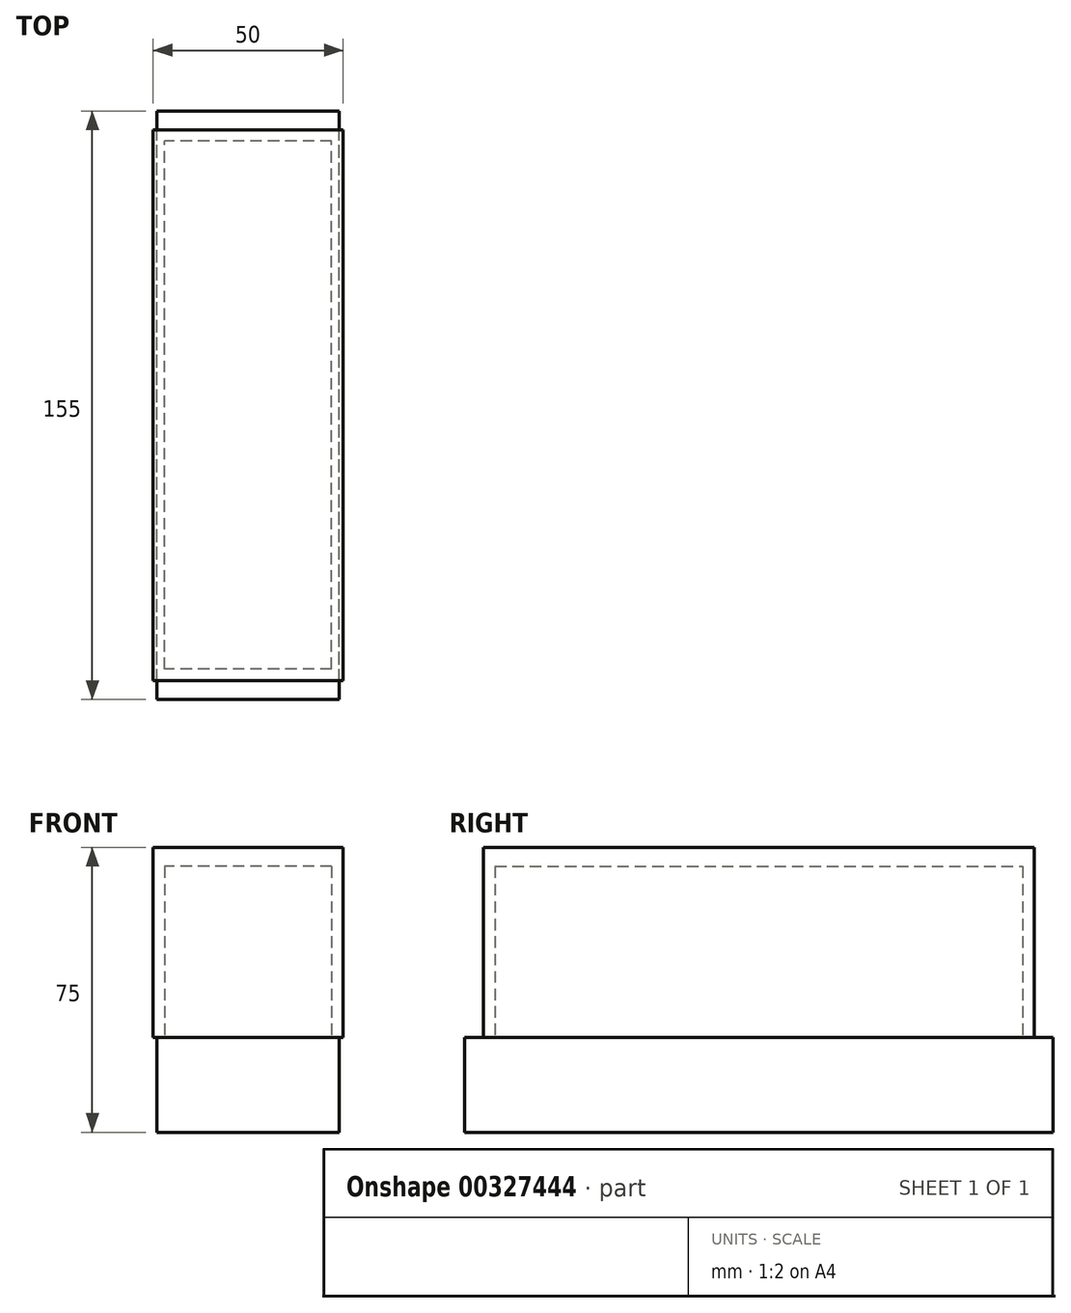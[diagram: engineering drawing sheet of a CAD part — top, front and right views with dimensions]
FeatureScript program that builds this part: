
annotation { "Feature Type Name" : "Feature", "Feature Type Description" : "" }
export const myFeature = defineFeature(function(context is Context, id is Id, definition is map)
    precondition{}
    {
        {
            var Q0;
            Q0=qCreatedBy(makeId("Top.planeOp"),FACE);
            var sketch = newSketch(context, id + "F0", { "sketchPlane" : qUnion([Q0])});
            skLineSegment(sketch, "E0.bottom", {"start": v(22, -69.5) * mm, "end": v(-22, -69.5) * mm});
            skLineSegment(sketch, "E0.top", {"start": v(22, 69.5) * mm, "end": v(-22, 69.5) * mm});
            skLineSegment(sketch, "E0.left", {"start": v(22, -69.5) * mm, "end": v(22, 69.5) * mm});
            skLineSegment(sketch, "E0.right", {"start": v(-22, -69.5) * mm, "end": v(-22, 69.5) * mm});
            skPoint(sketch, "E0.middle", {"position": v(0, 0) * mm});
            skLineSegment(sketch, "E1", {"start": v(0, 69.5) * mm, "end": v(0, -69.5) * mm, "construction": true});
            skLineSegment(sketch, "E2", {"start": v(-22, 0) * mm, "end": v(22, 0) * mm, "construction": true});
            skSolve(sketch);
        }
        {
            var Q0;
            Q0=makeQuery(id+"F0.imprint","IMPRINT",FACE,{"disambiguationData":[TD([[makeQuery(id+"F0.imprint","IMPRINT",EDGE,{"derivedFrom":sQuery(id+"F0.wireOp",EDGE,"E0.bottom")}),-1.0]])]});
            extrude(context, id + "F1", {"entities" : qUnion([Q0]), "depth" : 45 * mm});
        }
        {
            var Q0;
            Q0=qCreatedBy(makeId("Top.planeOp"),FACE);
            var sketch = newSketch(context, id + "F2", { "sketchPlane" : qUnion([Q0])});
            skLineSegment(sketch, "E3.bottom", {"start": v(25, -72.5) * mm, "end": v(-25, -72.5) * mm});
            skLineSegment(sketch, "E3.top", {"start": v(25, 72.5) * mm, "end": v(-25, 72.5) * mm});
            skLineSegment(sketch, "E3.left", {"start": v(25, -72.5) * mm, "end": v(25, 72.5) * mm});
            skLineSegment(sketch, "E3.right", {"start": v(-25, -72.5) * mm, "end": v(-25, 72.5) * mm});
            skPoint(sketch, "E3.middle", {"position": v(0, 0) * mm});
            skLineSegment(sketch, "E4", {"start": v(0, 72.5) * mm, "end": v(0, -72.5) * mm, "construction": true});
            skLineSegment(sketch, "E5", {"start": v(-25, 0) * mm, "end": v(25, 0) * mm, "construction": true});
            skSolve(sketch);
        }
        {
            var Q0;
            Q0=makeQuery(id+"F2.imprint","IMPRINT",FACE,{"disambiguationData":[TD([[makeQuery(id+"F2.imprint","IMPRINT",EDGE,{"derivedFrom":sQuery(id+"F2.wireOp",EDGE,"E3.bottom")}),-1.0]])]});
            extrude(context, id + "F3", {"entities" : qUnion([Q0]), "depth" : 50 * mm});
        }
        {
            var Q0;
            Q0=qCreatedBy(makeId("Top.planeOp"),FACE);
            var sketch = newSketch(context, id + "F4", { "sketchPlane" : qUnion([Q0])});
            skLineSegment(sketch, "E6.bottom", {"start": v(24, -77.5) * mm, "end": v(-24, -77.5) * mm});
            skLineSegment(sketch, "E6.top", {"start": v(24, 77.5) * mm, "end": v(-24, 77.5) * mm});
            skLineSegment(sketch, "E6.left", {"start": v(24, -77.5) * mm, "end": v(24, 77.5) * mm});
            skLineSegment(sketch, "E6.right", {"start": v(-24, -77.5) * mm, "end": v(-24, 77.5) * mm});
            skPoint(sketch, "E6.middle", {"position": v(0, 0) * mm});
            skSolve(sketch);
        }
        {
            var Q0;
            Q0=makeQuery(id+"F4.imprint","IMPRINT",FACE,{"disambiguationData":[TD([[makeQuery(id+"F4.imprint","IMPRINT",EDGE,{"derivedFrom":sQuery(id+"F4.wireOp",EDGE,"E6.bottom")}),-1.0]])]});
            extrude(context, id + "F5", {"entities" : qUnion([Q0]), "oppositeDirection" : true, "depth" : 25 * mm});
        }
    });
